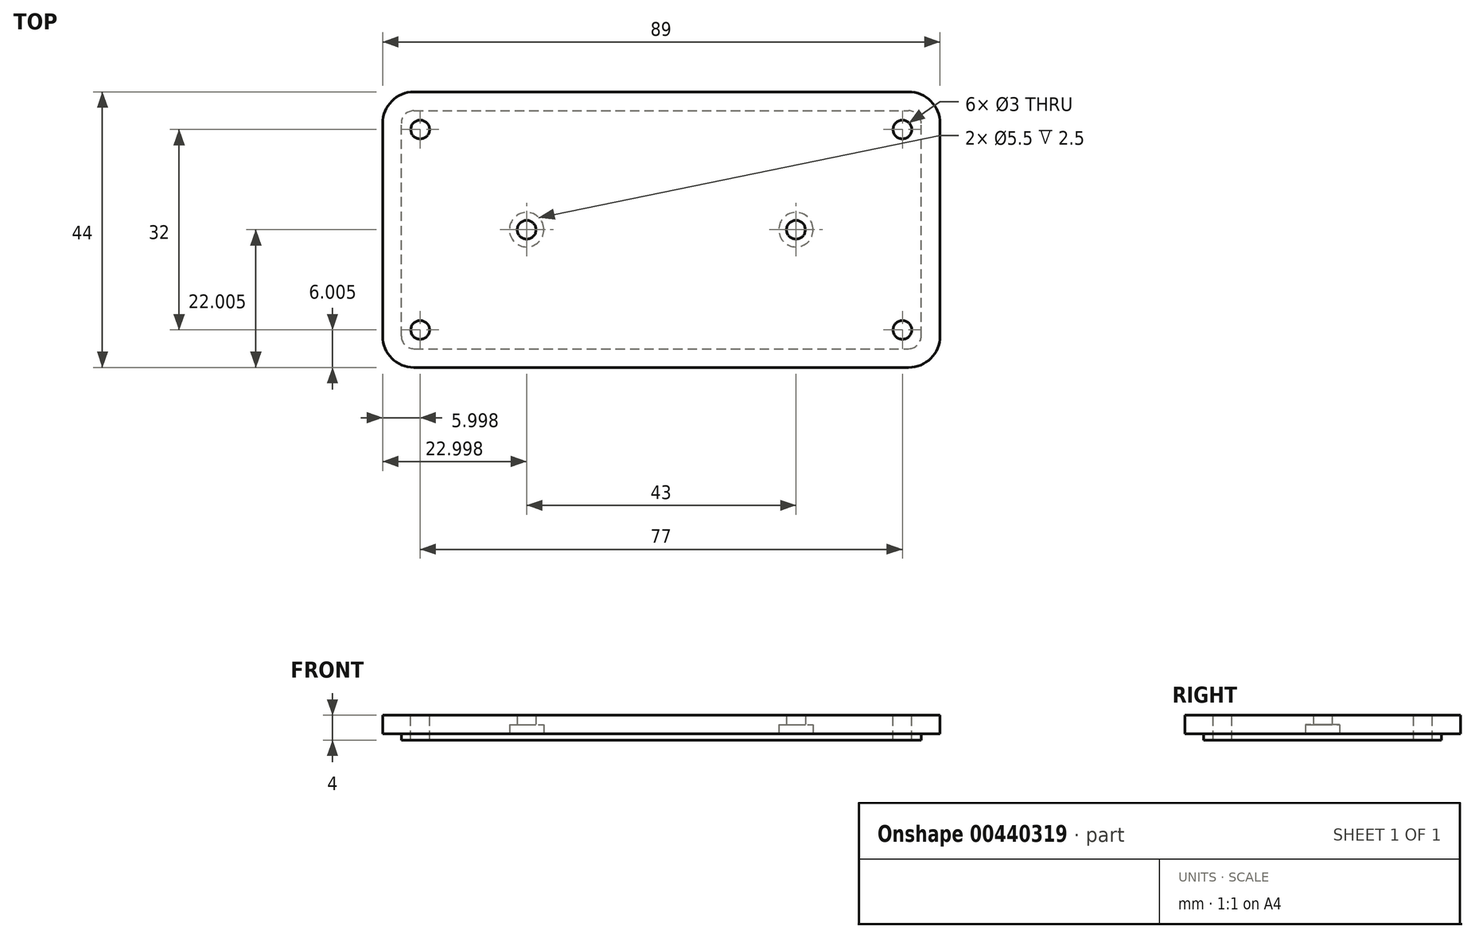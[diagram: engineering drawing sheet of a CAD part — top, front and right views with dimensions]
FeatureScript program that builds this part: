
annotation { "Feature Type Name" : "Feature", "Feature Type Description" : "" }
export const myFeature = defineFeature(function(context is Context, id is Id, definition is map)
    precondition{}
    {
        {
            var Q0;
            Q0=qCreatedBy(makeId("Top.planeOp"),FACE);
            var sketch = newSketch(context, id + "F0", { "sketchPlane" : qUnion([Q0])});
            skLineSegment(sketch, "E0.bottom", {"start": v(-41.95, 9.21) * mm, "end": v(43.05, 9.21) * mm});
            skLineSegment(sketch, "E0.top", {"start": v(-41.95, -30.79) * mm, "end": v(43.05, -30.79) * mm});
            skLineSegment(sketch, "E0.left", {"start": v(-41.95, 9.21) * mm, "end": v(-41.95, -30.79) * mm});
            skLineSegment(sketch, "E0.right", {"start": v(43.05, 9.21) * mm, "end": v(43.05, -30.79) * mm});
            skLineSegment(sketch, "E1.0", {"start": v(-43.95, -32.79) * mm, "end": v(45.05, -32.79) * mm});
            skLineSegment(sketch, "E1.1", {"start": v(-43.95, 11.21) * mm, "end": v(-43.95, -32.79) * mm});
            skLineSegment(sketch, "E1.2", {"start": v(-43.95, 11.21) * mm, "end": v(45.05, 11.21) * mm});
            skLineSegment(sketch, "E1.3", {"start": v(45.05, 11.21) * mm, "end": v(45.05, -32.79) * mm});
            skSolve(sketch);
        }
        {
            var Q0;
            Q0=makeQuery(id+"F0.imprint","IMPRINT",FACE,{"disambiguationData":[TD([[makeQuery(id+"F0.imprint","IMPRINT",EDGE,{"derivedFrom":sQuery(id+"F0.wireOp",EDGE,"E0.bottom")}),1.0]])]});
            var Q1;
            Q1=makeQuery(id+"F0.imprint","IMPRINT",FACE,{"disambiguationData":[TD([[makeQuery(id+"F0.imprint","IMPRINT",EDGE,{"derivedFrom":sQuery(id+"F0.wireOp",EDGE,"E0.bottom")}),-1.0]])]});
            extrude(context, id + "F1", {"entities" : qUnion([Q0, Q1]), "depth" : 3 * mm});
        }
        {
            var Q0;
            Q0=makeQuery(id+"F1.opExtrude","SWEPT_EDGE",EDGE,{"disambiguationData":[OSD([sQuery(id+"F0.wireOp",EDGE,"E1.1"),sQuery(id+"F0.wireOp",EDGE,"E1.2")])]});
            var Q1;
            Q1=makeQuery(id+"F1.opExtrude","SWEPT_EDGE",EDGE,{"disambiguationData":[OSD([sQuery(id+"F0.wireOp",EDGE,"E1.2"),sQuery(id+"F0.wireOp",EDGE,"E1.3")])]});
            var Q2;
            Q2=makeQuery(id+"F1.opExtrude","SWEPT_EDGE",EDGE,{"disambiguationData":[OSD([sQuery(id+"F0.wireOp",EDGE,"E1.0"),sQuery(id+"F0.wireOp",EDGE,"E1.3")])]});
            var Q3;
            Q3=makeQuery(id+"F1.opExtrude","SWEPT_EDGE",EDGE,{"disambiguationData":[OSD([sQuery(id+"F0.wireOp",EDGE,"E1.0"),sQuery(id+"F0.wireOp",EDGE,"E1.1")])]});
            fillet(context, id + "F2", {"entities" : qUnion([Q0, Q1, Q2, Q3]), "radius" : 5 * mm, "tangentPropagation" : true, "allowEdgeOverflow" : false});
        }
        {
            var Q0;
            Q0=makeQuery(id+"F1.opExtrude","CAP_FACE",FACE,{"disambiguationData":[OSD([sQuery(id+"F0.wireOp",EDGE,"E1.0"),sQuery(id+"F0.wireOp",EDGE,"E1.1"),sQuery(id+"F0.wireOp",EDGE,"E1.2"),sQuery(id+"F0.wireOp",EDGE,"E1.3")])],"isStart":true});
            var sketch = newSketch(context, id + "F3", { "sketchPlane" : qUnion([Q0])});
            skLineSegment(sketch, "E2.bottom", {"start": v(-43.95, 32.79) * mm, "end": v(45.05, 32.79) * mm});
            skLineSegment(sketch, "E2.top", {"start": v(-43.95, -11.21) * mm, "end": v(45.05, -11.21) * mm});
            skLineSegment(sketch, "E2.left", {"start": v(-43.95, 32.79) * mm, "end": v(-43.95, -11.21) * mm});
            skLineSegment(sketch, "E2.right", {"start": v(45.05, 32.79) * mm, "end": v(45.05, -11.21) * mm});
            skLineSegment(sketch, "E3.0", {"start": v(-40.95, 29.79) * mm, "end": v(42.05, 29.79) * mm});
            skLineSegment(sketch, "E3.1", {"start": v(-40.95, 29.79) * mm, "end": v(-40.95, -8.21) * mm});
            skLineSegment(sketch, "E3.2", {"start": v(-40.95, -8.21) * mm, "end": v(42.05, -8.21) * mm});
            skLineSegment(sketch, "E3.3", {"start": v(42.05, 29.79) * mm, "end": v(42.05, -8.21) * mm});
            skSolve(sketch);
        }
        {
            var Q0;
            Q0=makeQuery(id+"F3.imprint","IMPRINT",FACE,{"disambiguationData":[TD([[makeQuery(id+"F3.imprint","IMPRINT",EDGE,{"derivedFrom":sQuery(id+"F3.wireOp",EDGE,"E3.0")}),-1.0]])]});
            extrude(context, id + "F4", {"entities" : qUnion([Q0]), "operationType" : NewBodyOperationType.ADD, "depth" : 1 * mm});
        }
        {
            var Q0;
            Q0=makeQuery(id+"F4.opExtrude","SWEPT_EDGE",EDGE,{"disambiguationData":[OSD([sQuery(id+"F3.wireOp",EDGE,"E3.0"),sQuery(id+"F3.wireOp",EDGE,"E3.1")])]});
            var Q1;
            Q1=makeQuery(id+"F4.opExtrude","SWEPT_EDGE",EDGE,{"disambiguationData":[OSD([sQuery(id+"F3.wireOp",EDGE,"E3.1"),sQuery(id+"F3.wireOp",EDGE,"E3.2")])]});
            var Q2;
            Q2=makeQuery(id+"F4.opExtrude","SWEPT_EDGE",EDGE,{"disambiguationData":[OSD([sQuery(id+"F3.wireOp",EDGE,"E3.2"),sQuery(id+"F3.wireOp",EDGE,"E3.3")])]});
            var Q3;
            Q3=makeQuery(id+"F4.opExtrude","SWEPT_EDGE",EDGE,{"disambiguationData":[OSD([sQuery(id+"F3.wireOp",EDGE,"E3.0"),sQuery(id+"F3.wireOp",EDGE,"E3.3")])]});
            fillet(context, id + "F5", {"entities" : qUnion([Q0, Q1, Q2, Q3]), "radius" : 2 * mm, "tangentPropagation" : true, "allowEdgeOverflow" : false});
        }
        {
            var Q0;
            Q0=makeQuery(id+"F4.opExtrude","CAP_FACE",FACE,{"disambiguationData":[OSD([sQuery(id+"F0.wireOp",EDGE,"E1.0"),sQuery(id+"F0.wireOp",EDGE,"E1.1"),sQuery(id+"F0.wireOp",EDGE,"E1.2"),sQuery(id+"F0.wireOp",EDGE,"E1.3"),sQuery(id+"F10.wireOp",EDGE,"jefqAk4X-RZm9-SE6X-XYm3-7V9ZQbeEbyTu"),sQuery(id+"F10.wireOp",EDGE,"E11"),sQuery(id+"F3.wireOp",EDGE,"E3.0"),sQuery(id+"F3.wireOp",EDGE,"E3.1"),sQuery(id+"F3.wireOp",EDGE,"E3.2"),sQuery(id+"F3.wireOp",EDGE,"E3.3")])],"isStart":false});
            var sketch = newSketch(context, id + "F6", { "sketchPlane" : qUnion([Q0])});
            skLineSegment(sketch, "E4", {"start": v(-40.95, 10.79) * mm, "end": v(-20.95, 10.79) * mm});
            skCircle(sketch, "E5", {"center": v(-20.95, 10.79) * mm, "radius": 1.5 * mm});
            skLineSegment(sketch, "E6", {"start": v(42.05, 10.79) * mm, "end": v(22.05, 10.79) * mm});
            skCircle(sketch, "E7", {"center": v(22.05, 10.79) * mm, "radius": 1.5 * mm});
            skSolve(sketch);
        }
        {
            var Q0;
            Q0=makeQuery(id+"F6.imprint","IMPRINT",FACE,{"disambiguationData":[TD([[makeQuery(id+"F6.imprint","IMPRINT",EDGE,{"derivedFrom":sQuery(id+"F6.wireOp",EDGE,"E7")}),1.0]])]});
            var Q1;
            Q1=makeQuery(id+"F6.imprint","IMPRINT",FACE,{"disambiguationData":[TD([[makeQuery(id+"F6.imprint","IMPRINT",EDGE,{"derivedFrom":sQuery(id+"F6.wireOp",EDGE,"E5")}),1.0]])]});
            extrude(context, id + "F7", {"entities" : qUnion([Q0, Q1]), "operationType" : NewBodyOperationType.REMOVE, "oppositeDirection" : true, "depth" : 25 * mm});
        }
        {
            var Q0;
            Q0=makeQuery(id+"F4.opExtrude","CAP_FACE",FACE,{"disambiguationData":[OSD([sQuery(id+"F0.wireOp",EDGE,"E1.0"),sQuery(id+"F0.wireOp",EDGE,"E1.1"),sQuery(id+"F0.wireOp",EDGE,"E1.2"),sQuery(id+"F0.wireOp",EDGE,"E1.3"),sQuery(id+"F10.wireOp",EDGE,"jefqAk4X-RZm9-SE6X-XYm3-7V9ZQbeEbyTu"),sQuery(id+"F10.wireOp",EDGE,"E11"),sQuery(id+"F3.wireOp",EDGE,"E3.0"),sQuery(id+"F3.wireOp",EDGE,"E3.1"),sQuery(id+"F3.wireOp",EDGE,"E3.2"),sQuery(id+"F3.wireOp",EDGE,"E3.3")])],"isStart":false});
            var sketch = newSketch(context, id + "F8", { "sketchPlane" : qUnion([Q0])});
            skCircle(sketch, "E8", {"center": v(-20.95, 10.79) * mm, "radius": 2.75 * mm});
            skCircle(sketch, "E9", {"center": v(22.05, 10.79) * mm, "radius": 2.75 * mm});
            skSolve(sketch);
        }
        {
            var Q0;
            Q0=makeQuery(id+"F8.imprint","IMPRINT",FACE,{"disambiguationData":[TD([[makeQuery(id+"F8.imprint","IMPRINT",EDGE,{"derivedFrom":sQuery(id+"F8.wireOp",EDGE,"E8")}),1.0]])]});
            var Q1;
            Q1=makeQuery(id+"F8.imprint","IMPRINT",FACE,{"disambiguationData":[TD([[makeQuery(id+"F8.imprint","IMPRINT",EDGE,{"derivedFrom":sQuery(id+"F8.wireOp",EDGE,"E9")}),1.0]])]});
            extrude(context, id + "F9", {"entities" : qUnion([Q0, Q1]), "operationType" : NewBodyOperationType.REMOVE, "oppositeDirection" : true, "depth" : 2.5 * mm});
        }
        {
            var Q0;
            Q0=makeQuery(id+"F1.opExtrude","CAP_FACE",FACE,{"disambiguationData":[OSD([sQuery(id+"F0.wireOp",EDGE,"E1.0"),sQuery(id+"F0.wireOp",EDGE,"E1.1"),sQuery(id+"F0.wireOp",EDGE,"E1.2"),sQuery(id+"F0.wireOp",EDGE,"E1.3")])],"isStart":false});
            var sketch = newSketch(context, id + "F10", { "sketchPlane" : qUnion([Q0])});
            skLineSegment(sketch, "E10.top", {"start": v(-43.95, -26.79) * mm, "end": v(-37.95, -26.79) * mm});
            skLineSegment(sketch, "E10.right", {"start": v(-37.95, -32.79) * mm, "end": v(-37.95, -26.79) * mm});
            skCircle(sketch, "E11", {"center": v(-37.95, -26.79) * mm, "radius": 1.5 * mm});
            skLineSegment(sketch, "E12", {"start": v(-43.95, -10.79) * mm, "end": v(45.05, -10.79) * mm});
            skLineSegment(sketch, "E13", {"start": v(0.55, -32.79) * mm, "end": v(0.55, 11.21) * mm});
            skCircle(sketch, "E14.MirrorC", {"center": v(-37.95, 5.21) * mm, "radius": 1.5 * mm});
            skCircle(sketch, "E15.MirrorC", {"center": v(39.05, -26.79) * mm, "radius": 1.5 * mm});
            skCircle(sketch, "E16.MirrorC", {"center": v(39.05, 5.21) * mm, "radius": 1.5 * mm});
            skSolve(sketch);
        }
        {
            var Q0;
            Q0 = qSketchRegion(id + "F10", true);
            extrude(context, id + "F11", {"entities" : qUnion([Q0]), "operationType" : NewBodyOperationType.REMOVE, "oppositeDirection" : true, "depth" : 25 * mm});
        }
    });
